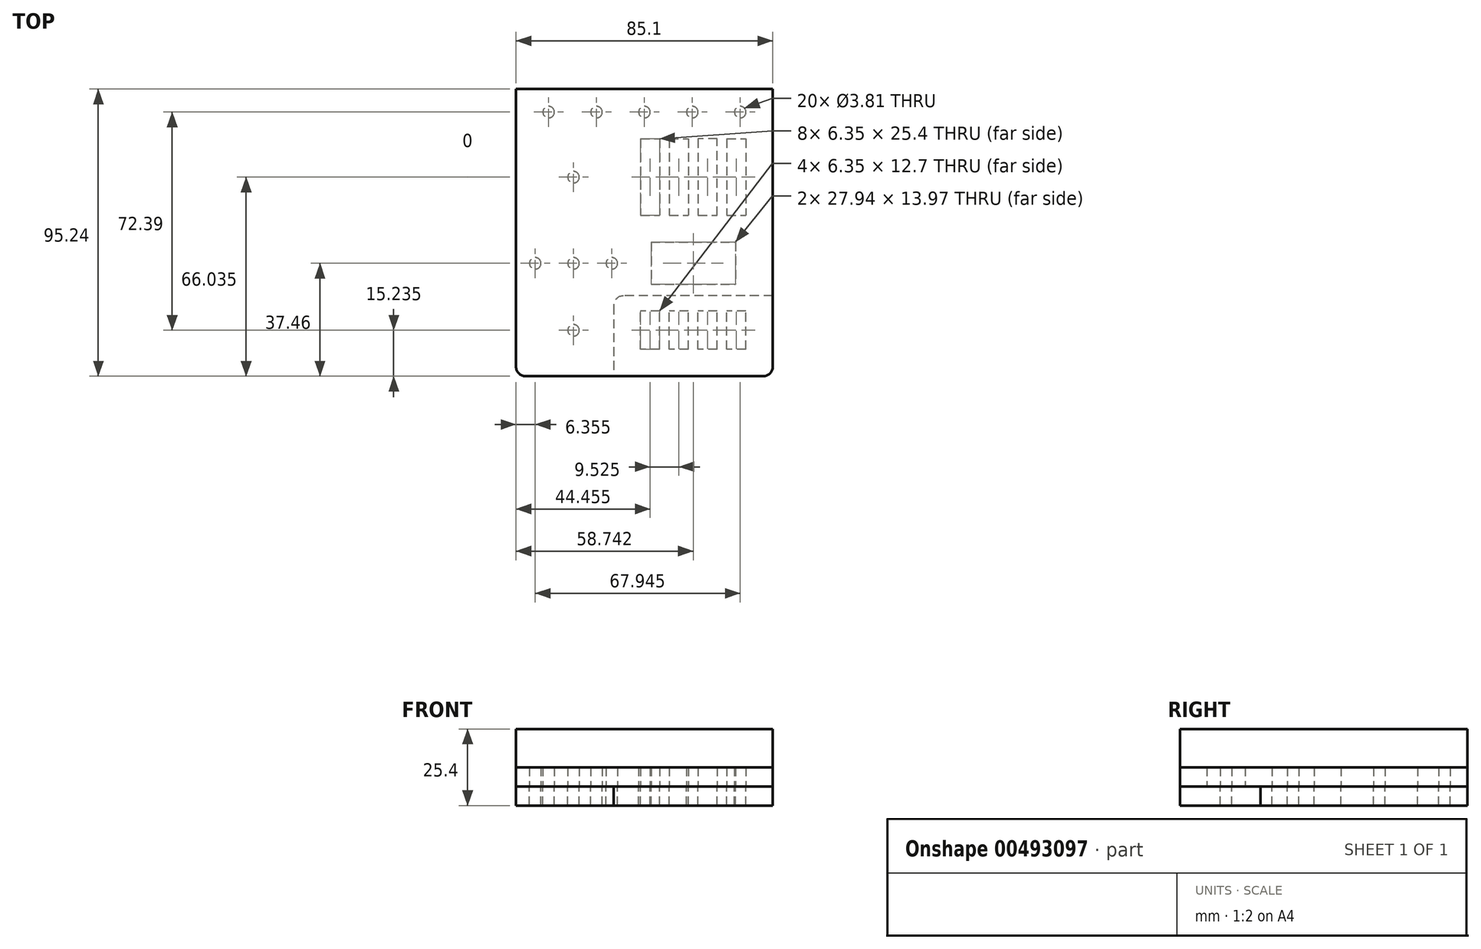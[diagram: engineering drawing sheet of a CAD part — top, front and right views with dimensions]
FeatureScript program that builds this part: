
annotation { "Feature Type Name" : "Feature", "Feature Type Description" : "" }
export const myFeature = defineFeature(function(context is Context, id is Id, definition is map)
    precondition{}
    {
        {
            var Q0;
            Q0=qCreatedBy(makeId("Top.planeOp"),FACE);
            var sketch = newSketch(context, id + "F0", { "sketchPlane" : qUnion([Q0])});
            skLineSegment(sketch, "E0.bottom", {"start": v(-42.55, 47.63) * mm, "end": v(42.55, 47.63) * mm});
            skLineSegment(sketch, "E0.top", {"start": v(-42.55, -47.63) * mm, "end": v(42.55, -47.63) * mm});
            skLineSegment(sketch, "E0.left", {"start": v(-42.55, 47.63) * mm, "end": v(-42.55, -47.63) * mm});
            skLineSegment(sketch, "E0.right", {"start": v(42.55, 47.63) * mm, "end": v(42.55, -47.63) * mm});
            skPoint(sketch, "E0.middle", {"position": v(0, 0) * mm});
            skSolve(sketch);
        }
        {
            var Q0;
            Q0=qSketchRegion(id+"F0",true);
            extrude(context, id + "F1", {"entities" : qUnion([Q0]), "depth" : 6.35 * mm});
        }
        {
            var Q0;
            Q0=qCreatedBy(makeId("Top.planeOp"),FACE);
            var sketch = newSketch(context, id + "F2", { "sketchPlane" : qUnion([Q0])});
            skCircle(sketch, "E1", {"center": v(-23.5, -32.39) * mm, "radius": 1.9 * mm});
            skCircle(sketch, "E2.0.1.0", {"center": v(-23.5, 18.41) * mm, "radius": 1.9 * mm});
            skLineSegment(sketch, "E2.direction1", {"start": v(-23.5, -32.39) * mm, "end": v(6.38, -32.39) * mm, "construction": true});
            skLineSegment(sketch, "E2.direction2", {"start": v(-23.5, -32.39) * mm, "end": v(-23.5, 18.41) * mm, "construction": true});
            skLineSegment(sketch, "E3.bottom", {"start": v(-1.27, -26.03) * mm, "end": v(5.08, -26.03) * mm});
            skLineSegment(sketch, "E3.top", {"start": v(-1.27, -38.73) * mm, "end": v(5.08, -38.73) * mm});
            skLineSegment(sketch, "E3.left", {"start": v(-1.27, -26.04) * mm, "end": v(-1.27, -38.74) * mm});
            skLineSegment(sketch, "E3.right", {"start": v(5.08, -26.04) * mm, "end": v(5.08, -38.74) * mm});
            skPoint(sketch, "E3.middle", {"position": v(1.9, -32.39) * mm});
            skLineSegment(sketch, "E4.bottom", {"start": v(-1.27, 24.77) * mm, "end": v(5.08, 24.77) * mm});
            skLineSegment(sketch, "E4.top", {"start": v(-1.27, 12.06) * mm, "end": v(5.08, 12.06) * mm});
            skLineSegment(sketch, "E4.left", {"start": v(-1.27, 24.76) * mm, "end": v(-1.27, 12.06) * mm});
            skLineSegment(sketch, "E4.right", {"start": v(5.08, 24.76) * mm, "end": v(5.08, 12.06) * mm});
            skPoint(sketch, "E4.middle", {"position": v(1.9, 18.41) * mm});
            skLineSegment(sketch, "E5.1.0.0", {"start": v(24.13, 24.77) * mm, "end": v(24.13, 12.06) * mm});
            skLineSegment(sketch, "E5.1.0.1", {"start": v(17.78, 12.06) * mm, "end": v(24.13, 12.06) * mm});
            skLineSegment(sketch, "E5.1.0.2", {"start": v(17.78, 24.76) * mm, "end": v(17.78, 12.06) * mm});
            skLineSegment(sketch, "E5.1.0.3", {"start": v(17.78, -26.03) * mm, "end": v(24.13, -26.03) * mm});
            skLineSegment(sketch, "E5.1.0.4", {"start": v(24.13, -26.04) * mm, "end": v(24.13, -38.74) * mm});
            skLineSegment(sketch, "E5.1.0.5", {"start": v(17.78, -26.04) * mm, "end": v(17.78, -38.74) * mm});
            skLineSegment(sketch, "E5.1.0.6", {"start": v(17.78, -38.73) * mm, "end": v(24.13, -38.73) * mm});
            skLineSegment(sketch, "E5.direction1", {"start": v(5.08, 12.06) * mm, "end": v(24.13, 12.06) * mm, "construction": true});
            skLineSegment(sketch, "E6", {"start": v(-23.5, 18.41) * mm, "end": v(-23.5, -32.39) * mm, "construction": true});
            skLineSegment(sketch, "E7", {"start": v(17.78, 24.77) * mm, "end": v(24.13, 24.77) * mm});
            skLineSegment(sketch, "E8", {"start": v(5.08, 18.41) * mm, "end": v(17.78, 18.41) * mm, "construction": true});
            skLineSegment(sketch, "E9", {"start": v(5.08, -32.39) * mm, "end": v(17.78, -32.39) * mm, "construction": true});
            skLineSegment(sketch, "E10.bottom", {"start": v(8.25, 24.76) * mm, "end": v(14.6, 24.76) * mm});
            skLineSegment(sketch, "E10.top", {"start": v(8.25, 12.06) * mm, "end": v(14.6, 12.06) * mm});
            skLineSegment(sketch, "E10.left", {"start": v(8.25, 24.76) * mm, "end": v(8.25, 12.06) * mm});
            skLineSegment(sketch, "E10.right", {"start": v(14.6, 24.76) * mm, "end": v(14.6, 12.06) * mm});
            skPoint(sketch, "E10.middle", {"position": v(11.43, 18.41) * mm});
            skLineSegment(sketch, "E11.bottom", {"start": v(8.25, -26.03) * mm, "end": v(14.6, -26.03) * mm});
            skLineSegment(sketch, "E11.top", {"start": v(8.25, -38.74) * mm, "end": v(14.6, -38.74) * mm});
            skLineSegment(sketch, "E11.left", {"start": v(8.25, -26.04) * mm, "end": v(8.25, -38.74) * mm});
            skLineSegment(sketch, "E11.right", {"start": v(14.6, -26.04) * mm, "end": v(14.6, -38.74) * mm});
            skPoint(sketch, "E11.middle", {"position": v(11.43, -32.39) * mm});
            skLineSegment(sketch, "E12.bottom", {"start": v(-1.27, 31.11) * mm, "end": v(5.08, 31.11) * mm});
            skLineSegment(sketch, "E12.top", {"start": v(-1.27, 5.71) * mm, "end": v(5.08, 5.71) * mm});
            skLineSegment(sketch, "E12.left", {"start": v(-1.27, 31.11) * mm, "end": v(-1.27, 5.71) * mm});
            skLineSegment(sketch, "E12.right", {"start": v(5.08, 31.12) * mm, "end": v(5.08, 5.71) * mm});
            skLineSegment(sketch, "E13.bottom", {"start": v(8.25, 31.11) * mm, "end": v(14.6, 31.11) * mm});
            skLineSegment(sketch, "E13.top", {"start": v(8.25, 5.71) * mm, "end": v(14.6, 5.71) * mm});
            skLineSegment(sketch, "E13.left", {"start": v(8.25, 31.12) * mm, "end": v(8.25, 5.71) * mm});
            skLineSegment(sketch, "E13.right", {"start": v(14.6, 31.11) * mm, "end": v(14.6, 5.71) * mm});
            skLineSegment(sketch, "E14", {"start": v(17.78, 18.41) * mm, "end": v(24.13, 18.41) * mm, "construction": true});
            skPoint(sketch, "E15", {"position": v(20.95, 18.41) * mm});
            skLineSegment(sketch, "E16", {"start": v(17.78, 5.71) * mm, "end": v(24.13, 5.71) * mm});
            skLineSegment(sketch, "E17", {"start": v(24.13, 5.71) * mm, "end": v(24.13, 31.11) * mm});
            skLineSegment(sketch, "E18", {"start": v(24.13, 31.11) * mm, "end": v(17.78, 31.11) * mm});
            skLineSegment(sketch, "E19", {"start": v(17.78, 31.12) * mm, "end": v(17.78, 5.71) * mm});
            skLineSegment(sketch, "E20.bottom", {"start": v(27.3, -26.03) * mm, "end": v(33.65, -26.03) * mm});
            skLineSegment(sketch, "E20.top", {"start": v(27.3, -38.73) * mm, "end": v(33.65, -38.73) * mm});
            skLineSegment(sketch, "E20.left", {"start": v(27.3, -26.03) * mm, "end": v(27.3, -38.74) * mm});
            skLineSegment(sketch, "E20.right", {"start": v(33.65, -26.03) * mm, "end": v(33.65, -38.74) * mm});
            skLineSegment(sketch, "E21.bottom", {"start": v(27.3, 31.11) * mm, "end": v(33.65, 31.11) * mm});
            skLineSegment(sketch, "E21.top", {"start": v(27.3, 5.71) * mm, "end": v(33.65, 5.71) * mm});
            skLineSegment(sketch, "E21.left", {"start": v(27.3, 31.11) * mm, "end": v(27.3, 5.71) * mm});
            skLineSegment(sketch, "E21.right", {"start": v(33.65, 31.11) * mm, "end": v(33.65, 5.71) * mm});
            skPoint(sketch, "E22", {"position": v(16.2, -10.16) * mm});
            skLineSegment(sketch, "E23.bottom", {"start": v(2.22, -3.17) * mm, "end": v(30.16, -3.17) * mm});
            skLineSegment(sketch, "E23.top", {"start": v(2.22, -17.14) * mm, "end": v(30.16, -17.14) * mm});
            skLineSegment(sketch, "E23.left", {"start": v(2.22, -3.17) * mm, "end": v(2.22, -17.14) * mm});
            skLineSegment(sketch, "E23.right", {"start": v(30.16, -3.17) * mm, "end": v(30.16, -17.15) * mm});
            skLineSegment(sketch, "E24", {"start": v(14.6, 5.71) * mm, "end": v(17.78, 5.71) * mm, "construction": true});
            skLineSegment(sketch, "E25", {"start": v(16.2, 5.71) * mm, "end": v(16.2, -26.03) * mm, "construction": true});
            skLineSegment(sketch, "E26", {"start": v(14.6, -26.03) * mm, "end": v(17.78, -26.03) * mm, "construction": true});
            skLineSegment(sketch, "E27", {"start": v(16.2, -10.16) * mm, "end": v(-37.78, -10.16) * mm, "construction": true});
            skCircle(sketch, "E28", {"center": v(-23.5, -10.16) * mm, "radius": 1.9 * mm});
            skCircle(sketch, "E29", {"center": v(-36.2, -10.16) * mm, "radius": 1.9 * mm});
            skCircle(sketch, "E30", {"center": v(-10.8, -10.16) * mm, "radius": 1.9 * mm});
            skCircle(sketch, "E31", {"center": v(-31.75, 40) * mm, "radius": 1.9 * mm});
            skCircle(sketch, "E32.1.0.0", {"center": v(-15.87, 40) * mm, "radius": 1.9 * mm});
            skCircle(sketch, "E32.2.0.0", {"center": v(0, 40) * mm, "radius": 1.9 * mm});
            skCircle(sketch, "E32.3.0.0", {"center": v(15.88, 40) * mm, "radius": 1.9 * mm});
            skCircle(sketch, "E32.4.0.0", {"center": v(31.75, 40) * mm, "radius": 1.9 * mm});
            skLineSegment(sketch, "E32.direction1", {"start": v(-31.75, 40) * mm, "end": v(-15.87, 40) * mm, "construction": true});
            skLineSegment(sketch, "E33", {"start": v(-31.75, 40) * mm, "end": v(-42.55, 40) * mm, "construction": true});
            skLineSegment(sketch, "E34", {"start": v(31.75, 40) * mm, "end": v(42.55, 40) * mm, "construction": true});
            skLineSegment(sketch, "E35.0", {"start": v(42.55, 47.63) * mm, "end": v(42.55, -47.63) * mm, "construction": true});
            skLineSegment(sketch, "E36.0", {"start": v(-42.55, 47.63) * mm, "end": v(-42.55, -47.63) * mm, "construction": true});
            skSolve(sketch);
        }
        {
            var Q0;
            Q0=qSketchRegion(id+"F2",true);
            extrude(context, id + "F3", {"entities" : qUnion([Q0]), "operationType" : NewBodyOperationType.REMOVE, "endBound" : BoundingType.THROUGH_ALL, "depth" : 25.4 * mm});
        }
        {
            var Q0;
            Q0=qSketchRegion(id+"F2",true);
            extrude(context, id + "F4", {"entities" : qUnion([Q0]), "operationType" : NewBodyOperationType.REMOVE, "endBound" : BoundingType.THROUGH_ALL, "oppositeDirection" : true, "depth" : 25.4 * mm});
        }
        {
            var Q0;
            Q0=makeQuery(id+"F1.opExtrude","CAP_FACE",FACE,{"disambiguationData":[OSD([sQuery(id+"F0.wireOp",EDGE,"E0.bottom"),sQuery(id+"F0.wireOp",EDGE,"E0.top"),sQuery(id+"F0.wireOp",EDGE,"E0.left"),sQuery(id+"F0.wireOp",EDGE,"E0.right")])],"isStart":true});
            extrude(context, id + "F5", {"entities" : qUnion([Q0]), "depth" : 6.35 * mm});
        }
        {
            var Q0;
            Q0=makeQuery(id+"F5.opExtrude","CAP_FACE",FACE,{"disambiguationData":[OSD([sQuery(id+"F0.wireOp",EDGE,"E0.bottom"),sQuery(id+"F0.wireOp",EDGE,"E0.top"),sQuery(id+"F0.wireOp",EDGE,"E0.left"),sQuery(id+"F0.wireOp",EDGE,"E0.right")])],"isStart":false});
            var sketch = newSketch(context, id + "F6", { "sketchPlane" : qUnion([Q0])});
            skLineSegment(sketch, "E37.bottom", {"start": v(42.55, 20.95) * mm, "end": v(-10.16, 20.95) * mm});
            skLineSegment(sketch, "E37.top", {"start": v(42.55, 47.63) * mm, "end": v(-10.16, 47.63) * mm});
            skLineSegment(sketch, "E37.left", {"start": v(42.55, 20.96) * mm, "end": v(42.55, 47.63) * mm});
            skLineSegment(sketch, "E37.right", {"start": v(-10.16, 20.95) * mm, "end": v(-10.16, 47.63) * mm});
            skSolve(sketch);
        }
        {
            var Q0;
            Q0=makeQuery(id+"F6.imprint","IMPRINT",FACE,{"disambiguationData":[TD([[makeQuery(id+"F6.imprint","IMPRINT",EDGE,{"derivedFrom":sQuery(id+"F6.wireOp",EDGE,"E37.bottom")}),-1.0]])]});
            var Q1;
            Q1=qCreatedBy(makeId("Top.planeOp"),FACE);
            extrude(context, id + "F7", {"entities" : qUnion([Q0]), "operationType" : NewBodyOperationType.REMOVE, "endBound" : BoundingType.UP_TO_SURFACE, "oppositeDirection" : true, "endBoundEntityFace" : qUnion([Q1]), "depth" : 25.4 * mm});
        }
        {
            var Q0;
            Q0=makeQuery(id+"F7.boolean.opBoolean","COPY",EDGE,{"derivedFrom":makeQuery(id+"F7.opExtrude","SWEPT_EDGE",EDGE,{"disambiguationData":[OSD([sQuery(id+"F0.wireOp",EDGE,"E0.top"),sQuery(id+"F6.wireOp",EDGE,"E37.top"),sQuery(id+"F6.wireOp",EDGE,"E37.right")])]})});
            var Q1;
            Q1=makeQuery(id+"F7.boolean.opBoolean","COPY",EDGE,{"derivedFrom":makeQuery(id+"F7.opExtrude","SWEPT_EDGE",EDGE,{"disambiguationData":[OSD([sQuery(id+"F6.wireOp",EDGE,"E37.bottom"),sQuery(id+"F6.wireOp",EDGE,"E37.right")])]})});
            var Q2;
            Q2=makeQuery(id+"F1.opExtrude","SWEPT_EDGE",EDGE,{"disambiguationData":[OSD([sQuery(id+"F0.wireOp",EDGE,"E0.top"),sQuery(id+"F0.wireOp",EDGE,"E0.right")])]});
            var Q3;
            Q3=makeQuery(id+"F7.boolean.opBoolean","COPY",EDGE,{"derivedFrom":makeQuery(id+"F7.opExtrude","SWEPT_EDGE",EDGE,{"disambiguationData":[OSD([sQuery(id+"F0.wireOp",EDGE,"E0.right"),sQuery(id+"F6.wireOp",EDGE,"E37.bottom"),sQuery(id+"F6.wireOp",EDGE,"E37.left")])]})});
            var Q4;
            Q4=makeQuery(id+"F1.opExtrude","SWEPT_EDGE",EDGE,{"disambiguationData":[OSD([sQuery(id+"F0.wireOp",EDGE,"E0.top"),sQuery(id+"F0.wireOp",EDGE,"E0.left")])]});
            var Q5;
            Q5=makeQuery(id+"F5.opExtrude","SWEPT_EDGE",EDGE,{"disambiguationData":[OSD([sQuery(id+"F0.wireOp",EDGE,"E0.top"),sQuery(id+"F0.wireOp",EDGE,"E0.left")])]});
            fillet(context, id + "F8", {"entities" : qUnion([Q0, Q1, Q2, Q3, Q4, Q5]), "radius" : 3.17 * mm, "tangentPropagation" : true, "allowEdgeOverflow" : false});
        }
        {
            var Q0;
            Q0=makeQuery(id+"F1.opExtrude","CAP_FACE",FACE,{"disambiguationData":[OSD([sQuery(id+"F0.wireOp",EDGE,"E0.bottom"),sQuery(id+"F0.wireOp",EDGE,"E0.top"),sQuery(id+"F0.wireOp",EDGE,"E0.left"),sQuery(id+"F0.wireOp",EDGE,"E0.right")])],"isStart":false});
            var sketch = newSketch(context, id + "F9", { "sketchPlane" : qUnion([Q0])});
            skLineSegment(sketch, "E38.0", {"start": v(-42.55, 47.63) * mm, "end": v(-42.55, -44.45) * mm});
            skPoint(sketch, "E39.0", {"position": v(-41.62, -46.7) * mm});
            skLineSegment(sketch, "E40.0", {"start": v(-39.37, -47.63) * mm, "end": v(39.37, -47.63) * mm});
            skLineSegment(sketch, "E41.0", {"start": v(42.55, 47.63) * mm, "end": v(42.55, -44.45) * mm});
            skPoint(sketch, "E42.0", {"position": v(41.62, -46.7) * mm});
            skLineSegment(sketch, "E43.0", {"start": v(-42.55, 47.63) * mm, "end": v(42.55, 47.63) * mm});
            skArc(sketch, "E44.0", {"start": v(39.37, -47.63) * mm, "mid": v(41.62, -46.7) * mm, "end": v(42.55, -44.45) * mm});
            skArc(sketch, "E45.0", {"start": v(-42.55, -44.45) * mm, "mid": v(-41.62, -46.7) * mm, "end": v(-39.37, -47.63) * mm});
            skSolve(sketch);
        }
        {
            var Q0;
            Q0 = qSketchRegion(id + "F9", true);
            extrude(context, id + "F10", {"entities" : qUnion([Q0]), "depth" : 12.7 * mm});
        }
    });
